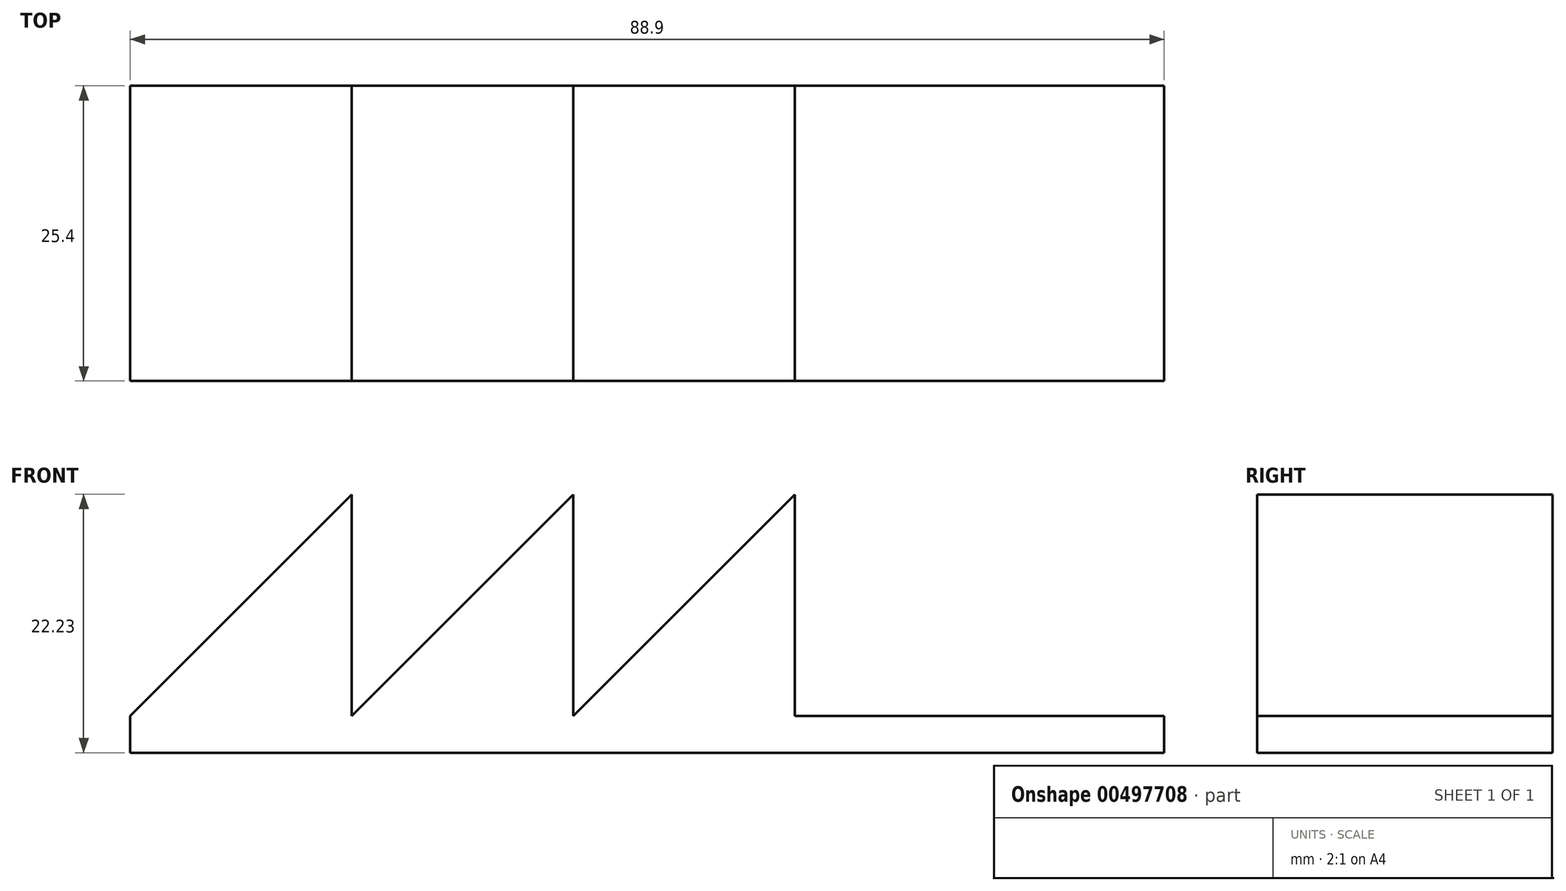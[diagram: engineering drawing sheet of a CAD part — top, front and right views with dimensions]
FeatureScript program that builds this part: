
annotation { "Feature Type Name" : "Feature", "Feature Type Description" : "" }
export const myFeature = defineFeature(function(context is Context, id is Id, definition is map)
    precondition{}
    {
        {
            var Q0;
            Q0=qCreatedBy(makeId("Front.planeOp"),FACE);
            var sketch = newSketch(context, id + "F0", { "sketchPlane" : qUnion([Q0])});
            skLineSegment(sketch, "E0.bottom", {"start": v(44.45, -1.59) * mm, "end": v(-44.45, -1.59) * mm});
            skLineSegment(sketch, "E0.top", {"start": v(44.45, 1.59) * mm, "end": v(12.7, 1.59) * mm});
            skLineSegment(sketch, "E0.left", {"start": v(44.45, -1.59) * mm, "end": v(44.45, 1.59) * mm});
            skLineSegment(sketch, "E0.right", {"start": v(-44.45, -1.59) * mm, "end": v(-44.45, 1.59) * mm});
            skPoint(sketch, "E0.middle", {"position": v(0, 0) * mm});
            skLineSegment(sketch, "E1.right", {"start": v(-25.4, 1.59) * mm, "end": v(-25.4, 20.64) * mm});
            skLineSegment(sketch, "E2", {"start": v(-44.45, 1.59) * mm, "end": v(-25.4, 20.64) * mm});
            skLineSegment(sketch, "E3.1.0.0", {"start": v(-6.35, 1.59) * mm, "end": v(-6.35, 20.64) * mm});
            skLineSegment(sketch, "E3.1.0.1", {"start": v(-25.4, 1.59) * mm, "end": v(-6.35, 20.64) * mm});
            skLineSegment(sketch, "E3.2.0.0", {"start": v(12.7, 1.59) * mm, "end": v(12.7, 20.64) * mm});
            skLineSegment(sketch, "E3.2.0.1", {"start": v(-6.35, 1.59) * mm, "end": v(12.7, 20.64) * mm});
            skSolve(sketch);
        }
        {
            var Q0;
            Q0 = qSketchRegion(id + "F0", true);
            extrude(context, id + "F1", {"entities" : qUnion([Q0]), "depth" : 25.4 * mm, "offsetDistance" : 25.4 * mm});
        }
    });
